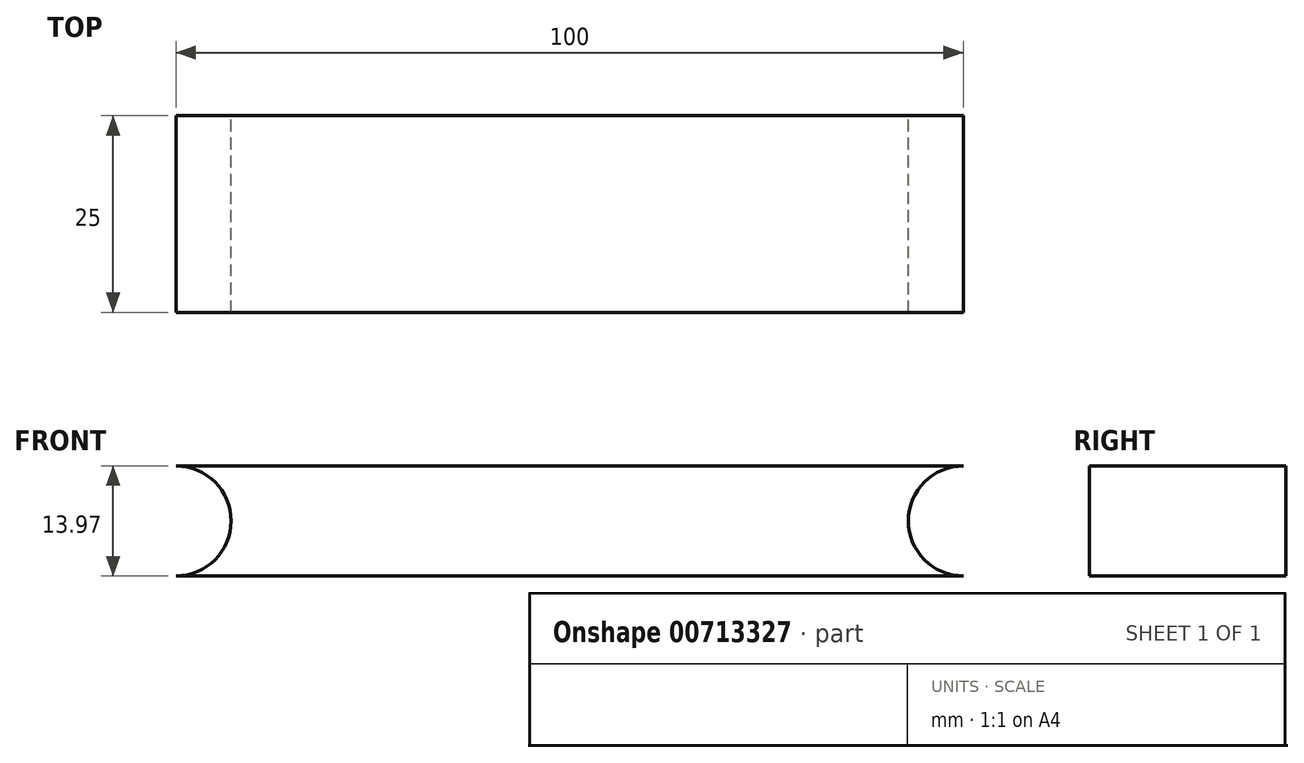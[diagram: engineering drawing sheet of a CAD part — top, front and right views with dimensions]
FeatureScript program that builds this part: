
annotation { "Feature Type Name" : "Feature", "Feature Type Description" : "" }
export const myFeature = defineFeature(function(context is Context, id is Id, definition is map)
    precondition{}
    {
        {
            var Q0;
            Q0=qCreatedBy(makeId("Front.planeOp"),FACE);
            var sketch = newSketch(context, id + "F0", { "sketchPlane" : qUnion([Q0])});
            skLineSegment(sketch, "E0.bottom", {"start": v(0, 0) * mm, "end": v(100, 0) * mm});
            skLineSegment(sketch, "E0.top", {"start": v(0, 13.97) * mm, "end": v(100, 13.97) * mm});
            skLineSegment(sketch, "E0.left", {"start": v(0, 0) * mm, "end": v(0, 13.97) * mm});
            skLineSegment(sketch, "E0.right", {"start": v(100, 0) * mm, "end": v(100, 13.97) * mm});
            skCircle(sketch, "E1", {"center": v(0, 6.98) * mm, "radius": 6.98 * mm});
            skCircle(sketch, "E2", {"center": v(100, 6.98) * mm, "radius": 6.98 * mm});
            skSolve(sketch);
        }
        {
            var Q0;
            {var subQ0=sQuery(id+"F0.wireOp",EDGE,"E0.bottom");Q0=makeQuery(id+"F0.imprint","IMPRINT",FACE,{"disambiguationData":[TD([[makeQuery(id+"F0.imprint","IMPRINT",EDGE,{"derivedFrom":subQ0}),1.0]])]});}
            extrude(context, id + "F1", {"entities" : qUnion([Q0]), "depth" : 25 * mm, "offsetDistance" : 25 * mm});
        }
    });
